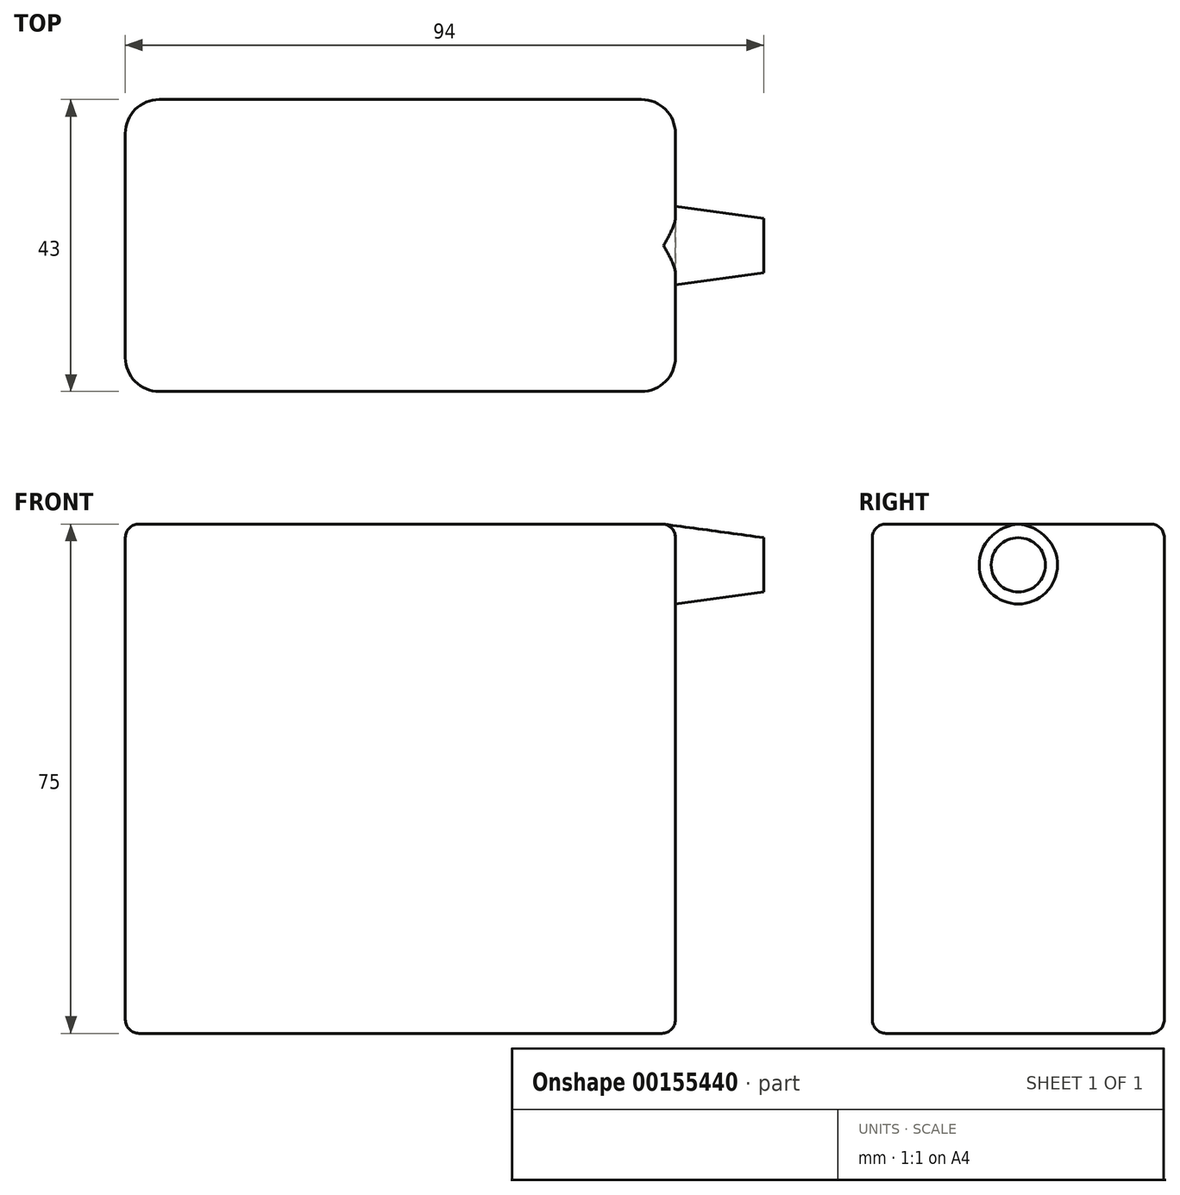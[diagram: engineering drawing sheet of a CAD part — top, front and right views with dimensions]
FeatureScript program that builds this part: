
annotation { "Feature Type Name" : "Feature", "Feature Type Description" : "" }
export const myFeature = defineFeature(function(context is Context, id is Id, definition is map)
    precondition{}
    {
        {
            var Q0;
            Q0=qCreatedBy(makeId("Top.planeOp"),FACE);
            var sketch = newSketch(context, id + "F0", { "sketchPlane" : qUnion([Q0])});
            skLineSegment(sketch, "E0.bottom", {"start": v(-35.5, 21.5) * mm, "end": v(35.5, 21.5) * mm});
            skLineSegment(sketch, "E0.top", {"start": v(-35.5, -21.5) * mm, "end": v(35.5, -21.5) * mm});
            skLineSegment(sketch, "E0.left", {"start": v(-40.5, 16.5) * mm, "end": v(-40.5, -16.5) * mm});
            skLineSegment(sketch, "E0.right", {"start": v(40.5, 16.5) * mm, "end": v(40.5, -16.5) * mm});
            skPoint(sketch, "E1.visualSharp", {"position": v(-40.5, 21.5) * mm});
            skArc(sketch, "E1.filletArc", {"start": v(-35.5, 21.5) * mm, "mid": v(-39.04, 20.04) * mm, "end": v(-40.5, 16.5) * mm});
            skPoint(sketch, "E2.visualSharp", {"position": v(40.5, 21.5) * mm});
            skArc(sketch, "E2.filletArc", {"start": v(40.5, 16.5) * mm, "mid": v(39.04, 20.04) * mm, "end": v(35.5, 21.5) * mm});
            skPoint(sketch, "E3.visualSharp", {"position": v(40.5, -21.5) * mm});
            skArc(sketch, "E3.filletArc", {"start": v(35.5, -21.5) * mm, "mid": v(39.04, -20.04) * mm, "end": v(40.5, -16.5) * mm});
            skPoint(sketch, "E4.visualSharp", {"position": v(-40.5, -21.5) * mm});
            skArc(sketch, "E4.filletArc", {"start": v(-40.5, -16.5) * mm, "mid": v(-39.04, -20.04) * mm, "end": v(-35.5, -21.5) * mm});
            skSolve(sketch);
        }
        {
            var Q0;
            Q0 = qSketchRegion(id + "F0", true);
            extrude(context, id + "F1", {"entities" : qUnion([Q0]), "depth" : 75 * mm});
        }
        {
            var Q0;
            Q0=makeQuery(id+"F1.opExtrude","CAP_FACE",FACE,{"disambiguationData":[OSD([sQuery(id+"F0.wireOp",EDGE,"E0.bottom"),sQuery(id+"F0.wireOp",EDGE,"E0.top"),sQuery(id+"F0.wireOp",EDGE,"E0.left"),sQuery(id+"F0.wireOp",EDGE,"E0.right"),sQuery(id+"F0.wireOp",EDGE,"E1.filletArc"),sQuery(id+"F0.wireOp",EDGE,"E2.filletArc"),sQuery(id+"F0.wireOp",EDGE,"E3.filletArc"),sQuery(id+"F0.wireOp",EDGE,"E4.filletArc")])],"isStart":false});
            var Q1;
            Q1=makeQuery(id+"F1.opExtrude","CAP_FACE",FACE,{"disambiguationData":[OSD([sQuery(id+"F0.wireOp",EDGE,"E0.bottom"),sQuery(id+"F0.wireOp",EDGE,"E0.top"),sQuery(id+"F0.wireOp",EDGE,"E0.left"),sQuery(id+"F0.wireOp",EDGE,"E0.right"),sQuery(id+"F0.wireOp",EDGE,"E1.filletArc"),sQuery(id+"F0.wireOp",EDGE,"E2.filletArc"),sQuery(id+"F0.wireOp",EDGE,"E3.filletArc"),sQuery(id+"F0.wireOp",EDGE,"E4.filletArc")])],"isStart":true});
            fillet(context, id + "F2", {"entities" : qUnion([Q0, Q1]), "radius" : 2 * mm, "tangentPropagation" : true, "allowEdgeOverflow" : false});
        }
        {
            var Q0;
            Q0=qCreatedBy(makeId("Front.planeOp"),FACE);
            var sketch = newSketch(context, id + "F3", { "sketchPlane" : qUnion([Q0])});
            skLineSegment(sketch, "E5.0", {"start": v(40.5, 73) * mm, "end": v(40.5, 2) * mm, "construction": true});
            skArc(sketch, "E6.0", {"start": v(38.5, 75) * mm, "mid": v(39.91, 74.41) * mm, "end": v(40.5, 73) * mm, "construction": true});
            skLineSegment(sketch, "E7", {"start": v(40.5, 68.98) * mm, "end": v(53.5, 68.98) * mm});
            skLineSegment(sketch, "E8", {"start": v(53.5, 68.98) * mm, "end": v(53.5, 72.98) * mm});
            skLineSegment(sketch, "E9", {"start": v(53.5, 72.98) * mm, "end": v(38.77, 74.98) * mm});
            skLineSegment(sketch, "E10", {"start": v(38.77, 74.98) * mm, "end": v(40.5, 68.98) * mm});
            skSolve(sketch);
        }
        {
            var Q0;
            Q0 = qSketchRegion(id + "F3", true);
            var Q1;
            Q1=sQuery(id+"F3.wireOp",EDGE,"E7");
            revolve(context, id + "F4", {"operationType" : NewBodyOperationType.ADD, "entities" : qUnion([Q0]), "axis" : qUnion([Q1]), "revolveType" : RevolveType.FULL});
        }
    });
